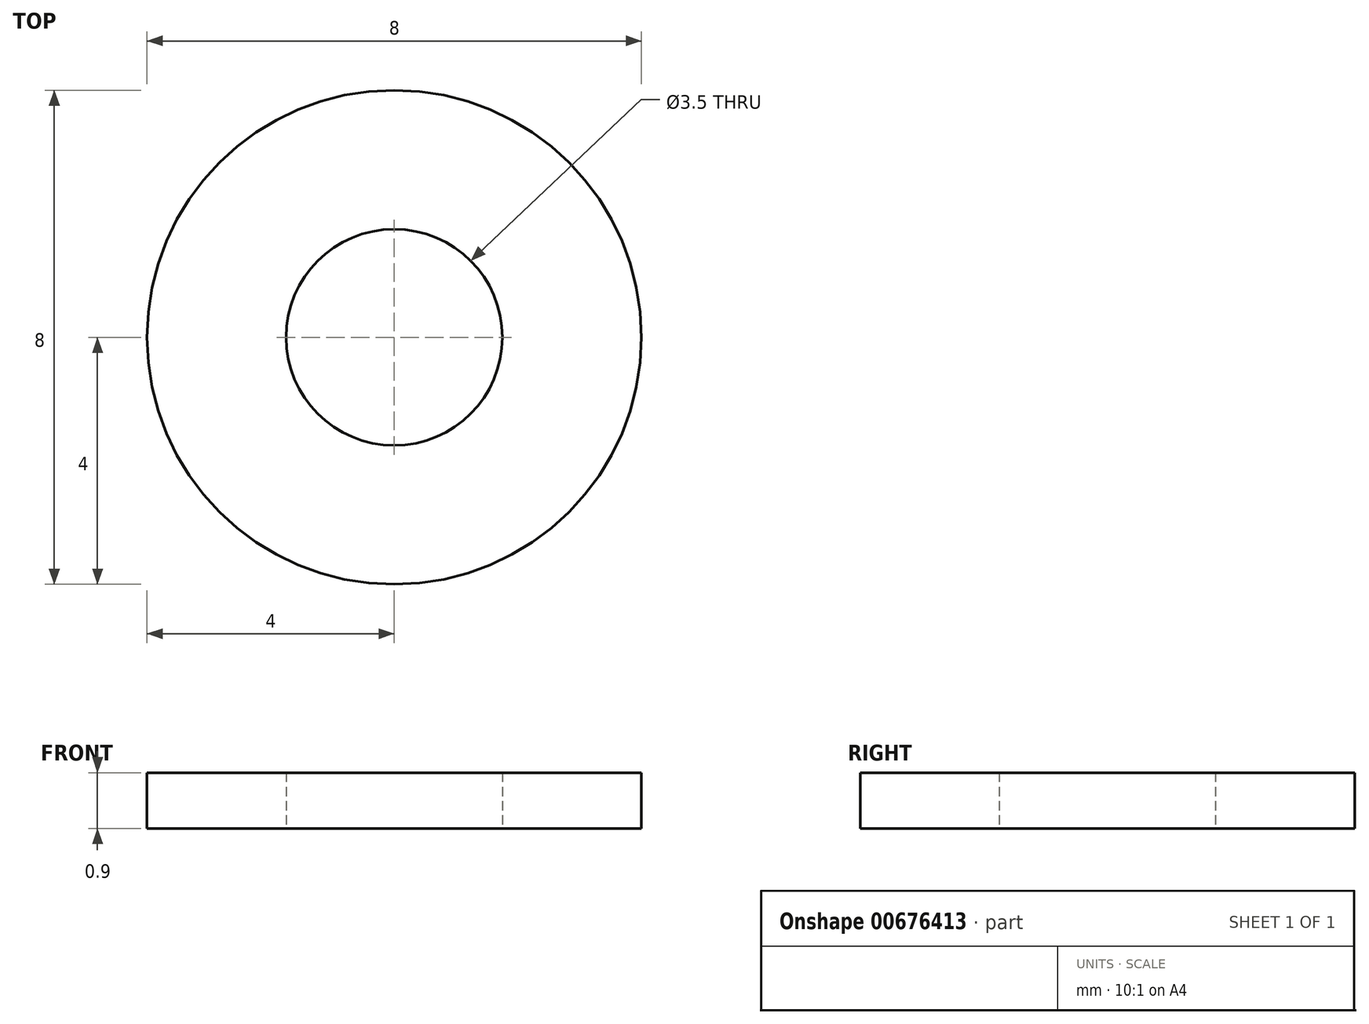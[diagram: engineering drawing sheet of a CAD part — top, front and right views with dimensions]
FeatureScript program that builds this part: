
annotation { "Feature Type Name" : "Feature", "Feature Type Description" : "" }
export const myFeature = defineFeature(function(context is Context, id is Id, definition is map)
    precondition{}
    {
        {
            var Q0;
            Q0=qCreatedBy(makeId("Top.planeOp"),FACE);
            var sketch = newSketch(context, id + "F0", { "sketchPlane" : qUnion([Q0])});
            skCircle(sketch, "E0", {"center": v(0, 0) * mm, "radius": 1.75 * mm});
            skCircle(sketch, "E1", {"center": v(0, 0) * mm, "radius": 4 * mm});
            skSolve(sketch);
        }
        {
            var Q0;
            Q0=makeQuery(id+"F0.imprint","IMPRINT",FACE,{"disambiguationData":[TD([[makeQuery(id+"F0.imprint","IMPRINT",EDGE,{"derivedFrom":sQuery(id+"F0.wireOp",EDGE,"E0")}),-1.0]])]});
            extrude(context, id + "F1", {"entities" : qUnion([Q0]), "flatOperationType" : FlatOperationType.REMOVE, "depth" : 0.9 * mm, "offsetDistance" : 25 * mm, "domain" : OperationDomain.MODEL, "symmetric" : true});
        }
    });
